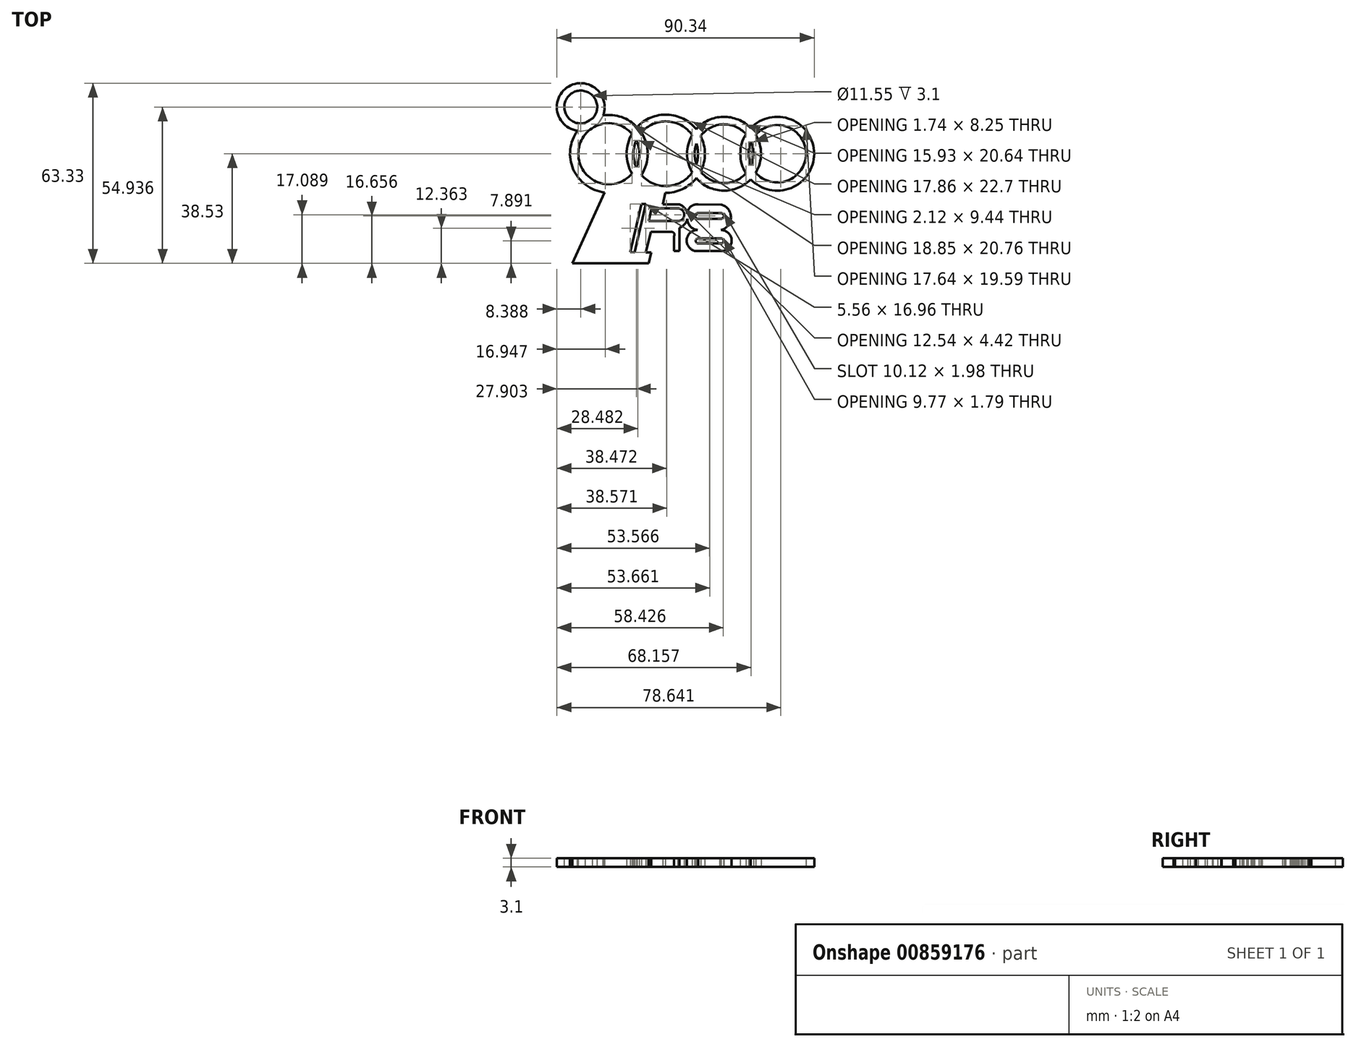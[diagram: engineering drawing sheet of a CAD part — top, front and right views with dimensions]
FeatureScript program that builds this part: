
annotation { "Feature Type Name" : "Feature", "Feature Type Description" : "" }
export const myFeature = defineFeature(function(context is Context, id is Id, definition is map)
    precondition{}
    {
        {
            var Q0;
            Q0=qCreatedBy(makeId("Top.planeOp"),FACE);
            var sketch = newSketch(context, id + "F0", { "sketchPlane" : qUnion([Q0])});
            skArc(sketch, "E0", {"start": v(-30.55, 9.36) * mm, "mid": v(-54.09, 0) * mm, "end": v(-30.55, -9.36) * mm});
            skArc(sketch, "E1", {"start": v(-30.55, -9.36) * mm, "mid": v(-19.97, -13.74) * mm, "end": v(-9.74, -8.57) * mm});
            skArc(sketch, "E2", {"start": v(-11.2, 6.55) * mm, "mid": v(-12.98, 0) * mm, "end": v(-11.2, -6.55) * mm});
            skArc(sketch, "E3", {"start": v(7.69, 6.9) * mm, "mid": v(5.7, 0) * mm, "end": v(7.69, -6.9) * mm});
            skArc(sketch, "E4", {"start": v(-32.33, 6.99) * mm, "mid": v(-51.18, 0) * mm, "end": v(-32.33, -6.99) * mm});
            skArc(sketch, "E5", {"start": v(-29.06, -7.47) * mm, "mid": v(-19.9, -11.35) * mm, "end": v(-11.2, -6.55) * mm});
            skArc(sketch, "E6", {"start": v(-9.7, 3.56) * mm, "mid": v(-10.33, 0) * mm, "end": v(-9.7, -3.56) * mm});
            skArc(sketch, "E7", {"start": v(9.47, 4.13) * mm, "mid": v(8.59, 0) * mm, "end": v(9.47, -4.13) * mm});
            skArc(sketch, "E8.trimOffspring", {"start": v(-8.24, -6.23) * mm, "mid": v(-0.43, -10.32) * mm, "end": v(7.69, -6.9) * mm});
            skArc(sketch, "E9.trimOffspring", {"start": v(-9.74, -8.57) * mm, "mid": v(-0.3, -12.97) * mm, "end": v(9.34, -9) * mm});
            skArc(sketch, "E10.trimOffspring", {"start": v(7.69, 6.9) * mm, "mid": v(-0.43, 10.32) * mm, "end": v(-8.24, 6.23) * mm});
            skArc(sketch, "E11.trimOffspring", {"start": v(9.34, 9) * mm, "mid": v(-0.3, 12.97) * mm, "end": v(-9.74, 8.57) * mm});
            skArc(sketch, "E12.trimOffspring", {"start": v(9.47, -4.13) * mm, "mid": v(10.33, 0) * mm, "end": v(9.47, 4.13) * mm});
            skArc(sketch, "E13.trimOffspring", {"start": v(11.12, -6.69) * mm, "mid": v(12.98, 0) * mm, "end": v(11.12, 6.69) * mm});
            skLineSegment(sketch, "E14", {"start": v(-41.98, -13.54) * mm, "end": v(-20.62, -13.75) * mm});
            skLineSegment(sketch, "E15", {"start": v(-20.62, -13.75) * mm, "end": v(-23.87, -27.5) * mm});
            skLineSegment(sketch, "E16", {"start": v(-26.48, -38.53) * mm, "end": v(-53.23, -38.53) * mm});
            skLineSegment(sketch, "E17", {"start": v(-53.23, -38.53) * mm, "end": v(-41.98, -13.54) * mm});
            skLineSegment(sketch, "E18", {"start": v(-23.57, -26.23) * mm, "end": v(-16.13, -26.23) * mm});
            skLineSegment(sketch, "E19", {"start": v(-16.13, -26.23) * mm, "end": v(-16.13, -34.2) * mm});
            skPoint(sketch, "E20.end.orphan", {"position": v(-30.43, -34.2) * mm});
            skLineSegment(sketch, "E21", {"start": v(-26.8, -26.23) * mm, "end": v(-28.8, -34.65) * mm});
            skLineSegment(sketch, "E22", {"start": v(-28.8, -34.65) * mm, "end": v(-31.45, -34.65) * mm});
            skLineSegment(sketch, "E23", {"start": v(-31.45, -34.65) * mm, "end": v(-27.44, -17.69) * mm});
            skLineSegment(sketch, "E24", {"start": v(-27.44, -17.69) * mm, "end": v(-15.7, -17.8) * mm});
            skLineSegment(sketch, "E25", {"start": v(-23.57, -26.23) * mm, "end": v(-26.8, -26.23) * mm});
            skLineSegment(sketch, "E26", {"start": v(-25.45, -19.23) * mm, "end": v(-26.5, -23.65) * mm});
            skLineSegment(sketch, "E27", {"start": v(-26.5, -23.65) * mm, "end": v(-16.3, -23.65) * mm});
            skLineSegment(sketch, "E28", {"start": v(-25.45, -19.23) * mm, "end": v(-16.3, -19.23) * mm});
            skArc(sketch, "E29", {"start": v(-16.3, -23.65) * mm, "mid": v(-13.96, -21.44) * mm, "end": v(-16.3, -19.23) * mm});
            skArc(sketch, "E30", {"start": v(-15.7, -26.05) * mm, "mid": v(-13.88, -24.83) * mm, "end": v(-12.89, -22.88) * mm});
            skLineSegment(sketch, "E31", {"start": v(-15.7, -34.2) * mm, "end": v(-15.7, -26.05) * mm});
            skLineSegment(sketch, "E32", {"start": v(-16.13, -34.2) * mm, "end": v(-15.7, -34.2) * mm});
            skLineSegment(sketch, "E33", {"start": v(-27.44, -17.69) * mm, "end": v(-29, -17.69) * mm});
            skLineSegment(sketch, "E34", {"start": v(-29, -17.69) * mm, "end": v(-33, -34.6) * mm});
            skLineSegment(sketch, "E35", {"start": v(-33, -34.6) * mm, "end": v(-31.45, -34.65) * mm});
            skLineSegment(sketch, "E36", {"start": v(-25.66, -20.12) * mm, "end": v(-16.17, -20.12) * mm});
            skArc(sketch, "E37", {"start": v(-16.3, -23.65) * mm, "mid": v(-15.09, -21.93) * mm, "end": v(-16.17, -20.12) * mm});
            skLineSegment(sketch, "E38", {"start": v(-17.51, -28.85) * mm, "end": v(-17.51, -34.2) * mm});
            skLineSegment(sketch, "E39", {"start": v(-17.51, -34.2) * mm, "end": v(-16.13, -34.2) * mm});
            skArc(sketch, "E40", {"start": v(-17.51, -28.85) * mm, "mid": v(-17.56, -27.93) * mm, "end": v(-18.35, -27.5) * mm});
            skPoint(sketch, "E41.end.orphan", {"position": v(-6.58, -34.2) * mm});
            skArc(sketch, "E42", {"start": v(-12.89, -22.88) * mm, "mid": v(-11.75, -25.62) * mm, "end": v(-9.02, -26.8) * mm});
            skPoint(sketch, "E43.start.orphan", {"position": v(-6.58, -17.8) * mm});
            skPoint(sketch, "E44.end.orphan", {"position": v(2.51, -17.8) * mm});
            skPoint(sketch, "E45.end.orphan", {"position": v(1.2, -20.36) * mm});
            skPoint(sketch, "E46.end.orphan", {"position": v(1.2, -21.1) * mm});
            skPoint(sketch, "E46.start.orphan", {"position": v(0.63, -23.06) * mm});
            skPoint(sketch, "E47.orphan", {"position": v(-5.54, -23.06) * mm});
            skPoint(sketch, "E48.orphan", {"position": v(2.99, -26.05) * mm});
            skPoint(sketch, "E49.end.orphan", {"position": v(2.51, -34.2) * mm});
            skPoint(sketch, "E50.end.orphan", {"position": v(-9.02, -34.87) * mm});
            skPoint(sketch, "E51.start.orphan", {"position": v(-6.58, -26.05) * mm});
            skPoint(sketch, "E52.start.orphan", {"position": v(0.63, -31.55) * mm});
            skPoint(sketch, "E53.end.orphan", {"position": v(1.2, -28.79) * mm});
            skPoint(sketch, "E54.end.orphan", {"position": v(1.2, -31.55) * mm});
            skPoint(sketch, "E55.end.orphan", {"position": v(1.2, -23.06) * mm});
            skPoint(sketch, "E56.end.orphan", {"position": v(-5.54, -31.55) * mm});
            skPoint(sketch, "E56.start.orphan", {"position": v(-5.54, -28.84) * mm});
            skArc(sketch, "E57", {"start": v(-9.02, -26.8) * mm, "mid": v(-13.12, -30.5) * mm, "end": v(-9.02, -34.2) * mm});
            skArc(sketch, "E58", {"start": v(-9.02, -17.8) * mm, "mid": v(-11.67, -18.57) * mm, "end": v(-12.87, -21.06) * mm});
            skLineSegment(sketch, "E59", {"start": v(-9.02, -17.8) * mm, "end": v(-1.05, -17.87) * mm});
            skArc(sketch, "E60", {"start": v(-1.05, -26.8) * mm, "mid": v(2.45, -22.34) * mm, "end": v(-1.05, -17.87) * mm});
            skLineSegment(sketch, "E61", {"start": v(-9.02, -34.2) * mm, "end": v(-1.05, -34.2) * mm});
            skArc(sketch, "E62", {"start": v(-1.05, -34.2) * mm, "mid": v(2.65, -30.5) * mm, "end": v(-1.05, -26.8) * mm});
            skArc(sketch, "E63", {"start": v(-9.02, -20.89) * mm, "mid": v(-10.2, -21.93) * mm, "end": v(-8.9, -22.83) * mm});
            skLineSegment(sketch, "E64", {"start": v(-9.02, -20.89) * mm, "end": v(-1.05, -20.89) * mm});
            skArc(sketch, "E65", {"start": v(-1.05, -22.83) * mm, "mid": v(-0.07, -21.86) * mm, "end": v(-1.05, -20.89) * mm});
            skLineSegment(sketch, "E66", {"start": v(-8.9, -22.83) * mm, "end": v(-1.05, -22.83) * mm});
            skLineSegment(sketch, "E67", {"start": v(-10.1, -21.44) * mm, "end": v(-1.05, -21.44) * mm});
            skArc(sketch, "E68", {"start": v(-1.57, -22.83) * mm, "mid": v(-0.84, -22.32) * mm, "end": v(-1.05, -21.44) * mm});
            skArc(sketch, "E69", {"start": v(-8.9, -29.74) * mm, "mid": v(-9.92, -30.64) * mm, "end": v(-8.9, -31.53) * mm});
            skLineSegment(sketch, "E70", {"start": v(-8.9, -29.74) * mm, "end": v(-1.05, -29.74) * mm});
            skArc(sketch, "E71", {"start": v(-1.05, -31.53) * mm, "mid": v(-0.15, -30.64) * mm, "end": v(-1.05, -29.74) * mm});
            skLineSegment(sketch, "E72", {"start": v(-8.9, -31.53) * mm, "end": v(-1.05, -31.53) * mm});
            skLineSegment(sketch, "E73", {"start": v(-9.85, -30.27) * mm, "end": v(-1.05, -30.27) * mm});
            skArc(sketch, "E74", {"start": v(-1.56, -31.53) * mm, "mid": v(-0.85, -31.09) * mm, "end": v(-1.05, -30.27) * mm});
            skArc(sketch, "E75.trimOffspring", {"start": v(-12.87, -21.06) * mm, "mid": v(-13.86, -19.05) * mm, "end": v(-15.7, -17.8) * mm});
            skLineSegment(sketch, "E76", {"start": v(-25.75, -27.5) * mm, "end": v(-27.45, -34.68) * mm});
            skLineSegment(sketch, "E77", {"start": v(-27.45, -34.68) * mm, "end": v(-25.57, -34.68) * mm});
            skLineSegment(sketch, "E78.trimOffspring", {"start": v(-23.87, -27.5) * mm, "end": v(-18.35, -27.5) * mm});
            skLineSegment(sketch, "E79.trimOffspring", {"start": v(-25.57, -34.68) * mm, "end": v(-26.48, -38.53) * mm});
            skLineSegment(sketch, "E80", {"start": v(-23.87, -27.5) * mm, "end": v(-25.75, -27.5) * mm});
            skArc(sketch, "E81.trimOffspring", {"start": v(9.34, -9) * mm, "mid": v(31.64, 0) * mm, "end": v(9.34, 9) * mm});
            skArc(sketch, "E82.trimOffspring", {"start": v(11.12, -6.69) * mm, "mid": v(28.76, 0) * mm, "end": v(11.12, 6.69) * mm});
            skArc(sketch, "E83.trimOffspring", {"start": v(-11.2, 6.55) * mm, "mid": v(-19.9, 11.35) * mm, "end": v(-29.06, 7.47) * mm});
            skArc(sketch, "E84.trimOffspring", {"start": v(-9.74, 8.57) * mm, "mid": v(-19.97, 13.74) * mm, "end": v(-30.55, 9.36) * mm});
            skArc(sketch, "E85.trimOffspring", {"start": v(-9.7, -3.56) * mm, "mid": v(-9.12, 0) * mm, "end": v(-9.7, 3.56) * mm});
            skArc(sketch, "E86.trimOffspring", {"start": v(-8.24, -6.23) * mm, "mid": v(-6.74, 0) * mm, "end": v(-8.24, 6.23) * mm});
            skArc(sketch, "E87.trimOffspring", {"start": v(-30.83, 4.72) * mm, "mid": v(-31.86, 0) * mm, "end": v(-30.83, -4.72) * mm});
            skArc(sketch, "E88.trimOffspring", {"start": v(-32.33, 6.99) * mm, "mid": v(-34.23, 0) * mm, "end": v(-32.33, -6.99) * mm});
            skArc(sketch, "E89.trimOffspring", {"start": v(-30.83, -4.72) * mm, "mid": v(-29.74, 0) * mm, "end": v(-30.83, 4.72) * mm});
            skArc(sketch, "E90.trimOffspring", {"start": v(-29.06, -7.47) * mm, "mid": v(-26.83, 0) * mm, "end": v(-29.06, 7.47) * mm});
            skSolve(sketch);
        }
        {
            var Q0;
            Q0 = qSketchRegion(id + "F0", true);
            extrude(context, id + "F1", {"entities" : qUnion([Q0]), "depth" : 3 * mm, "offsetDistance" : 25 * mm});
        }
        {
            var Q0;
            Q0=makeQuery(id+"F1.opExtrude","CAP_FACE",FACE,{"disambiguationData":[OSD([sQuery(id+"F0.wireOp",EDGE,"E0"),sQuery(id+"F0.wireOp",EDGE,"E1"),sQuery(id+"F0.wireOp",EDGE,"E2"),sQuery(id+"F0.wireOp",EDGE,"E3"),sQuery(id+"F0.wireOp",EDGE,"E4"),sQuery(id+"F0.wireOp",EDGE,"E5"),sQuery(id+"F0.wireOp",EDGE,"E6"),sQuery(id+"F0.wireOp",EDGE,"E7"),sQuery(id+"F0.wireOp",EDGE,"E8.trimOffspring"),sQuery(id+"F0.wireOp",EDGE,"E9.trimOffspring"),sQuery(id+"F0.wireOp",EDGE,"E10.trimOffspring"),sQuery(id+"F0.wireOp",EDGE,"E11.trimOffspring"),sQuery(id+"F0.wireOp",EDGE,"E12.trimOffspring"),sQuery(id+"F0.wireOp",EDGE,"E13.trimOffspring"),sQuery(id+"F0.wireOp",EDGE,"E15"),sQuery(id+"F0.wireOp",EDGE,"E16"),sQuery(id+"F0.wireOp",EDGE,"E17"),sQuery(id+"F0.wireOp",EDGE,"E23"),sQuery(id+"F0.wireOp",EDGE,"E24"),sQuery(id+"F0.wireOp",EDGE,"E26"),sQuery(id+"F0.wireOp",EDGE,"E27"),sQuery(id+"F0.wireOp",EDGE,"E28"),sQuery(id+"F0.wireOp",EDGE,"E29"),sQuery(id+"F0.wireOp",EDGE,"E30"),sQuery(id+"F0.wireOp",EDGE,"E31"),sQuery(id+"F0.wireOp",EDGE,"E32"),sQuery(id+"F0.wireOp",EDGE,"E33"),sQuery(id+"F0.wireOp",EDGE,"E34"),sQuery(id+"F0.wireOp",EDGE,"E35"),sQuery(id+"F0.wireOp",EDGE,"E38"),sQuery(id+"F0.wireOp",EDGE,"E39"),sQuery(id+"F0.wireOp",EDGE,"E40"),sQuery(id+"F0.wireOp",EDGE,"E42"),sQuery(id+"F0.wireOp",EDGE,"E57"),sQuery(id+"F0.wireOp",EDGE,"E58"),sQuery(id+"F0.wireOp",EDGE,"E59"),sQuery(id+"F0.wireOp",EDGE,"E60"),sQuery(id+"F0.wireOp",EDGE,"E61"),sQuery(id+"F0.wireOp",EDGE,"E62"),sQuery(id+"F0.wireOp",EDGE,"E63"),sQuery(id+"F0.wireOp",EDGE,"E64"),sQuery(id+"F0.wireOp",EDGE,"E65"),sQuery(id+"F0.wireOp",EDGE,"E66"),sQuery(id+"F0.wireOp",EDGE,"E69"),sQuery(id+"F0.wireOp",EDGE,"E70"),sQuery(id+"F0.wireOp",EDGE,"E71"),sQuery(id+"F0.wireOp",EDGE,"E72"),sQuery(id+"F0.wireOp",EDGE,"E74"),sQuery(id+"F0.wireOp",EDGE,"E75.trimOffspring"),sQuery(id+"F0.wireOp",EDGE,"E76"),sQuery(id+"F0.wireOp",EDGE,"E77"),sQuery(id+"F0.wireOp",EDGE,"E78.trimOffspring"),sQuery(id+"F0.wireOp",EDGE,"E79.trimOffspring"),sQuery(id+"F0.wireOp",EDGE,"E80"),sQuery(id+"F0.wireOp",EDGE,"E81.trimOffspring"),sQuery(id+"F0.wireOp",EDGE,"E82.trimOffspring"),sQuery(id+"F0.wireOp",EDGE,"E83.trimOffspring"),sQuery(id+"F0.wireOp",EDGE,"E84.trimOffspring"),sQuery(id+"F0.wireOp",EDGE,"E85.trimOffspring"),sQuery(id+"F0.wireOp",EDGE,"E86.trimOffspring"),sQuery(id+"F0.wireOp",EDGE,"E87.trimOffspring"),sQuery(id+"F0.wireOp",EDGE,"E88.trimOffspring"),sQuery(id+"F0.wireOp",EDGE,"E89.trimOffspring"),sQuery(id+"F0.wireOp",EDGE,"E90.trimOffspring")])],"isStart":false});
            var sketch = newSketch(context, id + "F2", { "sketchPlane" : qUnion([Q0])});
            skCircle(sketch, "E91", {"center": v(-50.31, 16.4) * mm, "radius": 5.78 * mm});
            skCircle(sketch, "E92", {"center": v(-50.31, 16.4) * mm, "radius": 8.4 * mm});
            skSolve(sketch);
        }
        {
            var Q0;
            Q0 = qSketchRegion(id + "F2", true);
            extrude(context, id + "F3", {"entities" : qUnion([Q0]), "operationType" : NewBodyOperationType.ADD, "oppositeDirection" : true, "depth" : 3.1 * mm, "offsetDistance" : 25 * mm});
        }
    });
